# Revit family: QSC Core 8 Flex_Surface Mount
name_source: partatom
category: Generic Models
revit_build: Autodesk Revit 2017 (Build: 20190508_0315(x64)
units: mm (PartAtom-declared; Revit-internal decimal feet)

## family parameters
Can host rebar = No
Cut with Voids When Loaded = No
Host = Face
Part Type = Normal
Room Calculation Point = No
Round Connector Dimension = Use Diameter
Shared = No

## types (1)
- Core 8 Flex
    Default Elevation = 0.000"
    Depth = 11.280"
    Description = Q-SYS Network + Analog I/O Processor
    Face Depth = 0.079"
    Heat Load Active = 110
    Height = 1.720"
    Manufacturer = QSC
    Manufacturer URL = http://www.qsc.com
    Model = Core 8 Flex
    Power Active = 40
    Product Documentation Link = https://www.qsc.com
    Product Page URL = https://www.qsc.com
    Regulatory Compliance = FCC Part 68 / TIA-968-B; ES203 021, CE, RoHS; PTC200; NOM-151-SCTI; JATE; UL & C-UL Listed; AC; PSTN01; Industry Canada CS-03; AS/ACIF S002 & RCM; ANATEL Resolution 473
    Weight Product (kg) = 1.81
    Weight Product (lb) = 4
    Width = 8.660"

## geometry (parser evidence)
native form markers: Blend x5, Sweep x3
no freeform markers — native parametric forms only
